# Revit family: 80db4df2_960a_4fa5_abae_2372334b2c2c
name_source: partatom
category: Generic Models
revit_build: Autodesk Revit Architecture 2015 (Build: 20140606_1530(x64)
units: mm (PartAtom-declared; Revit-internal decimal feet)

## types (1)
- Default
    BIMobject category = Outside
    BOSUseNativeGeometries = 1
    Date of publishing = 6/14/2012
    Design country = Denmark
    Edition number = 2
    IFC Classification = Light Fixture
    Installation instructions = http://www.focus-lighting.dk
    Manufacturer country = Denmark
    Manufacturer name = Focus Lighting
    Material main = Silumin
    Material secondary = Glass
    Nominal height = 178
    Nominal width = 450
    Product Guid = 35e82266-d28c-4a64-975a-9998797e6db7
    Product SKU = 5703646922143
    Product data url = https://bimobject.com
    Product family = Outdoor
    Product group = Columns
    Product name = Nyx Lantern 450
    QR code = http://bimobject.com
    Technical description = http://www.focus-lighting.dk
    UNSPSC Code = 391016
    Weight Net (Kg) = 11
    Youtube clip = https://www.youtube.com

## geometry (parser evidence)
native form markers: Sweep x2
no freeform markers — native parametric forms only
